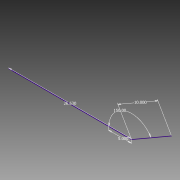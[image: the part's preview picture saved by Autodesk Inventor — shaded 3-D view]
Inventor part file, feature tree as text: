
AUTODESK INVENTOR PART (.ipt)
format: ipt  version: 2013 (Build 170138000, 138)  size: 61,952 bytes
history: native  units: in
note: dims shown in document units (in); Inventor stores cm internally (conversion verified against a paired STEP export)
features: sketch x1
ambient origin geometry x8: Origin, YZ Plane, XZ Plane, XY Plane, X Axis, Y Axis, Z Axis, Center Point
feature tree (1):
  sketch  "Sketch1"  dims[d0=26.63in d2=5.0in d3=150.0deg d4=10.0in]
